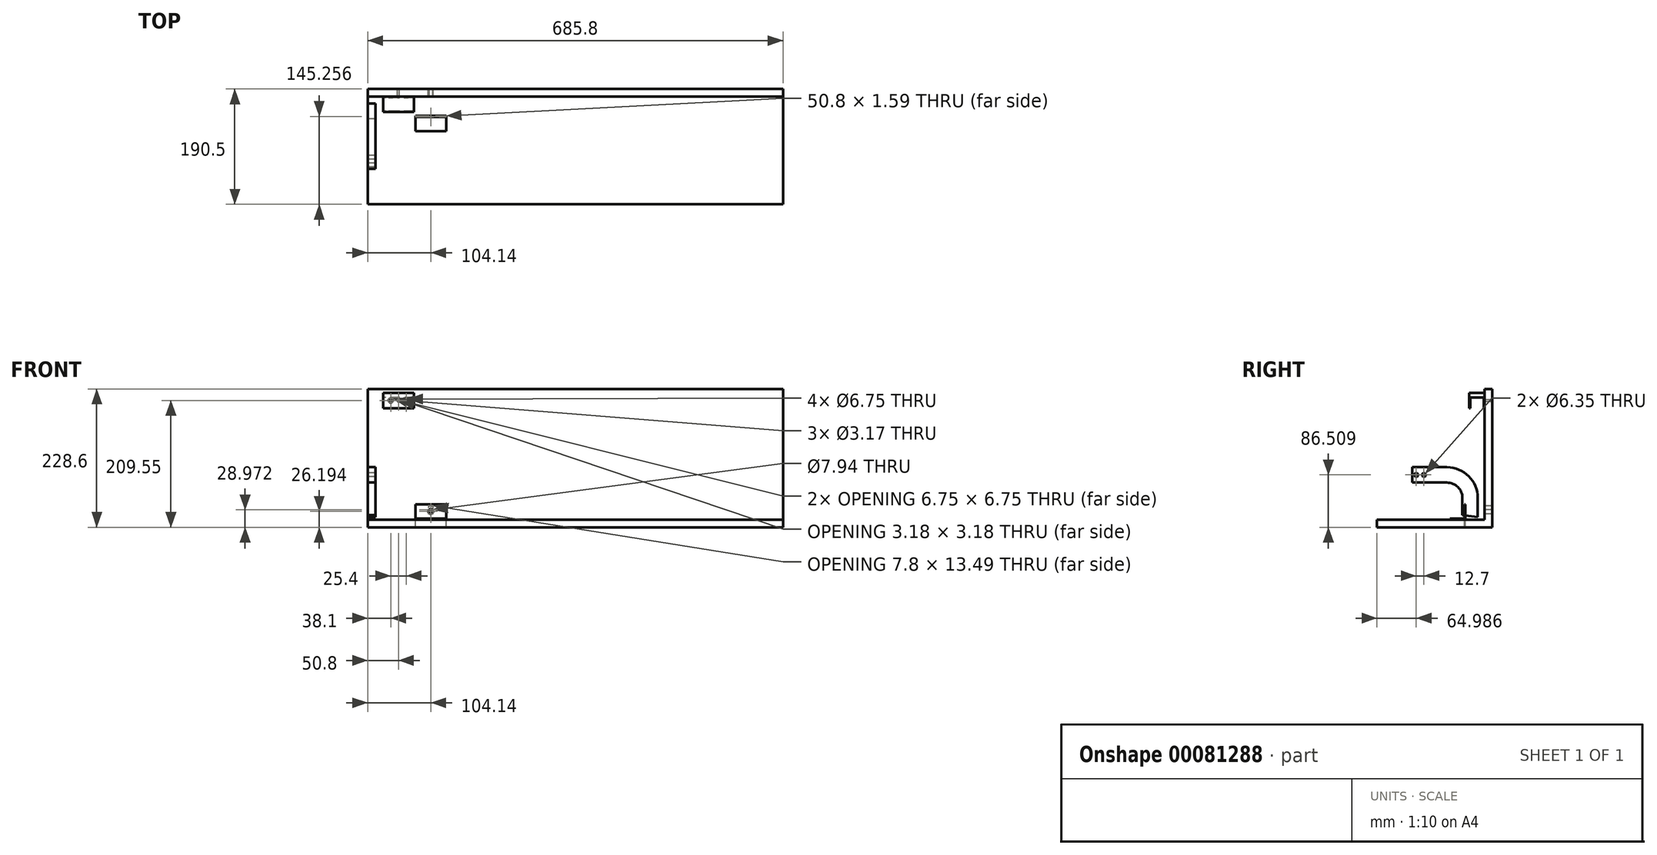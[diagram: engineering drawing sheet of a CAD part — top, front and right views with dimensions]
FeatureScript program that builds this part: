
annotation { "Feature Type Name" : "Feature", "Feature Type Description" : "" }
export const myFeature = defineFeature(function(context is Context, id is Id, definition is map)
    precondition{}
    {
        {
            var Q0;
            Q0=qCreatedBy(makeId("Front.planeOp"),FACE);
            var sketch = newSketch(context, id + "F0", { "sketchPlane" : qUnion([Q0])});
            skLineSegment(sketch, "E0.bottom", {"start": v(0, 0) * mm, "end": v(685.8, 0) * mm});
            skLineSegment(sketch, "E0.top", {"start": v(0, 215.9) * mm, "end": v(685.8, 215.9) * mm});
            skLineSegment(sketch, "E0.left", {"start": v(0, 0) * mm, "end": v(0, 215.9) * mm});
            skLineSegment(sketch, "E0.right", {"start": v(685.8, 0) * mm, "end": v(685.8, 215.9) * mm});
            skCircle(sketch, "E1", {"center": v(50.8, 196.85) * mm, "radius": 1.59 * mm});
            skCircle(sketch, "E2", {"center": v(104.14, 19.05) * mm, "radius": 3.97 * mm});
            skLineSegment(sketch, "E3.top", {"start": v(0, -12.7) * mm, "end": v(685.8, -12.7) * mm});
            skLineSegment(sketch, "E3.left", {"start": v(0, 0) * mm, "end": v(0, -12.7) * mm});
            skLineSegment(sketch, "E3.right", {"start": v(685.8, 0) * mm, "end": v(685.8, -12.7) * mm});
            skSolve(sketch);
        }
        {
            var Q0;
            Q0 = qSketchRegion(id + "F0", true);
            extrude(context, id + "F1", {"entities" : qUnion([Q0]), "depth" : 12.7 * mm});
        }
        {
            var Q0;
            Q0=qCreatedBy(makeId("Right.planeOp"),FACE);
            var sketch = newSketch(context, id + "F2", { "sketchPlane" : qUnion([Q0])});
            skLineSegment(sketch, "E4.top", {"start": v(-131.86, 61.1) * mm, "end": v(-74.77, 61.1) * mm});
            skLineSegment(sketch, "E4.left", {"start": v(-131.86, 86.5) * mm, "end": v(-131.86, 61.1) * mm});
            skLineSegment(sketch, "E5", {"start": v(-49.37, 35.7) * mm, "end": v(-49.37, 7.13) * mm});
            skLineSegment(sketch, "E6", {"start": v(-23.97, 4.36) * mm, "end": v(-49.37, 7.13) * mm});
            skPoint(sketch, "E7.visualSharp", {"position": v(-49.37, 61.1) * mm});
            skArc(sketch, "E7.filletArc", {"start": v(-49.37, 35.7) * mm, "mid": v(-56.8, 53.67) * mm, "end": v(-74.77, 61.1) * mm});
            skLineSegment(sketch, "E8.0", {"start": v(-23.97, 35.7) * mm, "end": v(-23.97, 4.36) * mm});
            skArc(sketch, "E8.1", {"start": v(-23.97, 35.7) * mm, "mid": v(-38.84, 71.63) * mm, "end": v(-74.77, 86.5) * mm});
            skLineSegment(sketch, "E8.2", {"start": v(-131.88, 86.5) * mm, "end": v(-74.77, 86.5) * mm});
            skPoint(sketch, "E9.orphan", {"position": v(-4.86, 2.27) * mm});
            skCircle(sketch, "E10", {"center": v(-125.51, 73.8) * mm, "radius": 3.18 * mm});
            skCircle(sketch, "E11", {"center": v(-112.81, 73.8) * mm, "radius": 3.18 * mm});
            skSolve(sketch);
        }
        {
            var Q0;
            Q0=makeQuery(id+"F2.imprint","IMPRINT",FACE,{"disambiguationData":[TD([[makeQuery(id+"F2.imprint","IMPRINT",EDGE,{"derivedFrom":sQuery(id+"F2.wireOp",EDGE,"E4.top")}),1.0]])]});
            extrude(context, id + "F3", {"entities" : qUnion([Q0]), "depth" : 12.7 * mm});
        }
        {
            var Q0;
            Q0=makeQuery(id+"F0.imprint","IMPRINT",FACE,{"disambiguationData":[TD([[makeQuery(id+"F0.imprint","IMPRINT",EDGE,{"derivedFrom":sQuery(id+"F0.wireOp",EDGE,"E0.bottom")}),-1.0]])]});
            extrude(context, id + "F4", {"entities" : qUnion([Q0]), "operationType" : NewBodyOperationType.ADD, "depth" : 190.5 * mm});
        }
        {
            var Q0;
            Q0=makeQuery(id+"F4.opExtrude","SWEPT_FACE",FACE,{"disambiguationData":[OSD([sQuery(id+"F0.wireOp",EDGE,"E0.bottom")])]});
            var sketch = newSketch(context, id + "F5", { "sketchPlane" : qUnion([Q0])});
            skLineSegment(sketch, "E12.bottom", {"start": v(78.74, -44.45) * mm, "end": v(129.54, -44.45) * mm});
            skLineSegment(sketch, "E12.top", {"start": v(78.74, -69.85) * mm, "end": v(129.54, -69.85) * mm});
            skLineSegment(sketch, "E12.left", {"start": v(78.74, -44.45) * mm, "end": v(78.74, -69.85) * mm});
            skLineSegment(sketch, "E12.right", {"start": v(129.54, -44.45) * mm, "end": v(129.54, -69.85) * mm});
            skSolve(sketch);
        }
        {
            var Q0;
            Q0 = qSketchRegion(id + "F5", true);
            extrude(context, id + "F6", {"entities" : qUnion([Q0]), "depth" : 1.59 * mm});
        }
        {
            var Q0;
            Q0=makeQuery(id+"F6.opExtrude","CAP_FACE",FACE,{"disambiguationData":[OSD([sQuery(id+"F5.wireOp",EDGE,"E12.bottom"),sQuery(id+"F5.wireOp",EDGE,"E12.top"),sQuery(id+"F5.wireOp",EDGE,"E12.left"),sQuery(id+"F5.wireOp",EDGE,"E12.right")])],"isStart":false});
            var sketch = newSketch(context, id + "F7", { "sketchPlane" : qUnion([Q0])});
            skLineSegment(sketch, "E13.bottom", {"start": v(78.74, -44.45) * mm, "end": v(129.54, -44.45) * mm});
            skLineSegment(sketch, "E13.top", {"start": v(78.74, -46.04) * mm, "end": v(129.54, -46.04) * mm});
            skLineSegment(sketch, "E13.left", {"start": v(78.74, -44.45) * mm, "end": v(78.74, -46.04) * mm});
            skLineSegment(sketch, "E13.right", {"start": v(129.54, -44.45) * mm, "end": v(129.54, -46.04) * mm});
            skSolve(sketch);
        }
        {
            var Q0;
            Q0 = qSketchRegion(id + "F7", true);
            var Q1;
            Q1 = qSketchRegion(id + "FHozlwFsfVEOZ7I_2", true);
            extrude(context, id + "F8", {"entities" : qUnion([Q0, Q1]), "operationType" : NewBodyOperationType.ADD, "depth" : 23.8 * mm});
        }
        {
            var Q0;
            Q0 = qSketchRegion(id + "F7", true);
            var Q1;
            Q1=sQuery(id+"FHozlwFsfVEOZ7I_2.wireOp",EDGE,"sIB5UJZw-k6Wk-qyg9-ZXtD-PutCMp7WBZc7");
            extrude(context, id + "F9", {"entities" : qUnion([Q0]), "operationType" : NewBodyOperationType.REMOVE, "surfaceEntities" : qUnion([Q1]), "endBound" : BoundingType.THROUGH_ALL, "oppositeDirection" : true, "depth" : 25.4 * mm});
        }
        {
            var Q0;
            Q0=makeQuery(id+"F1.opExtrude","CAP_FACE",FACE,{"disambiguationData":[OSD([sQuery(id+"F0.wireOp",EDGE,"E0.top"),sQuery(id+"F0.wireOp",EDGE,"E0.left"),sQuery(id+"F0.wireOp",EDGE,"E0.right"),sQuery(id+"F0.wireOp",EDGE,"E1"),sQuery(id+"F0.wireOp",EDGE,"E2"),sQuery(id+"F0.wireOp",EDGE,"E3.top"),sQuery(id+"F0.wireOp",EDGE,"E3.left"),sQuery(id+"F0.wireOp",EDGE,"E3.right")])],"isStart":false});
            var sketch = newSketch(context, id + "F10", { "sketchPlane" : qUnion([Q0])});
            skLineSegment(sketch, "E14.bottom", {"start": v(25.4, 209.55) * mm, "end": v(76.2, 209.55) * mm});
            skLineSegment(sketch, "E14.top", {"start": v(25.4, 184.15) * mm, "end": v(76.2, 184.15) * mm});
            skLineSegment(sketch, "E14.left", {"start": v(25.4, 209.55) * mm, "end": v(25.4, 184.15) * mm});
            skLineSegment(sketch, "E14.right", {"start": v(76.2, 209.55) * mm, "end": v(76.2, 184.15) * mm});
            skCircle(sketch, "E15", {"center": v(50.8, 196.85) * mm, "radius": 1.59 * mm});
            skCircle(sketch, "E16", {"center": v(38.1, 196.85) * mm, "radius": 3.37 * mm});
            skCircle(sketch, "E17", {"center": v(63.5, 196.85) * mm, "radius": 3.37 * mm});
            skSolve(sketch);
        }
        {
            var Q0;
            Q0 = qSketchRegion(id + "F10", true);
            extrude(context, id + "F11", {"entities" : qUnion([Q0]), "depth" : 25.4 * mm});
        }
        {
            var Q0;
            Q0=makeQuery(id+"F11.opExtrude","SWEPT_FACE",FACE,{"disambiguationData":[OSD([sQuery(id+"F10.wireOp",EDGE,"E14.left")])]});
            var sketch = newSketch(context, id + "F12", { "sketchPlane" : qUnion([Q0])});
            skLineSegment(sketch, "E18.0", {"start": v(36.51, 201.61) * mm, "end": v(14.29, 201.61) * mm});
            skLineSegment(sketch, "E19.0", {"start": v(36.51, 179.39) * mm, "end": v(14.29, 179.39) * mm});
            skLineSegment(sketch, "E20.0", {"start": v(14.29, 201.61) * mm, "end": v(14.29, 179.39) * mm});
            skLineSegment(sketch, "E21", {"start": v(36.51, 201.61) * mm, "end": v(36.51, 179.39) * mm});
            skSolve(sketch);
        }
        {
            var Q0;
            Q0=makeQuery(id+"F12.imprint","IMPRINT",FACE,{"disambiguationData":[TD([[makeQuery(id+"F12.imprint","IMPRINT",EDGE,{"derivedFrom":sQuery(id+"F12.wireOp",EDGE,"E18.0")}),1.0]])]});
            extrude(context, id + "F13", {"entities" : qUnion([Q0]), "operationType" : NewBodyOperationType.REMOVE, "endBound" : BoundingType.THROUGH_ALL, "oppositeDirection" : true, "depth" : 25.4 * mm});
        }
        {
            var Q0;
            Q0=makeQuery(id+"F8.opExtrude","SWEPT_FACE",FACE,{"disambiguationData":[OSD([sQuery(id+"F7.wireOp",EDGE,"E13.top")])]});
            var sketch = newSketch(context, id + "F14", { "sketchPlane" : qUnion([Q0])});
            skCircle(sketch, "E22", {"center": v(104.14, 13.5) * mm, "radius": 3.97 * mm});
            skLineSegment(sketch, "E23", {"start": v(78.74, 13.5) * mm, "end": v(129.54, 13.5) * mm, "construction": true});
            skLineSegment(sketch, "E24", {"start": v(104.14, 25.4) * mm, "end": v(104.14, 1.59) * mm, "construction": true});
            skSolve(sketch);
        }
        {
            var Q0;
            Q0=makeQuery(id+"F14.imprint","IMPRINT",FACE,{"disambiguationData":[TD([[makeQuery(id+"F14.imprint","IMPRINT",EDGE,{"derivedFrom":sQuery(id+"F14.wireOp",EDGE,"E22")}),1.0]])]});
            var Q1;
            Q1=sQuery(id+"F14.wireOp",EDGE,"E22");
            extrude(context, id + "F15", {"entities" : qUnion([Q0]), "operationType" : NewBodyOperationType.REMOVE, "surfaceEntities" : qUnion([Q1]), "endBound" : BoundingType.THROUGH_ALL, "oppositeDirection" : true, "depth" : 25.4 * mm});
        }
    });
